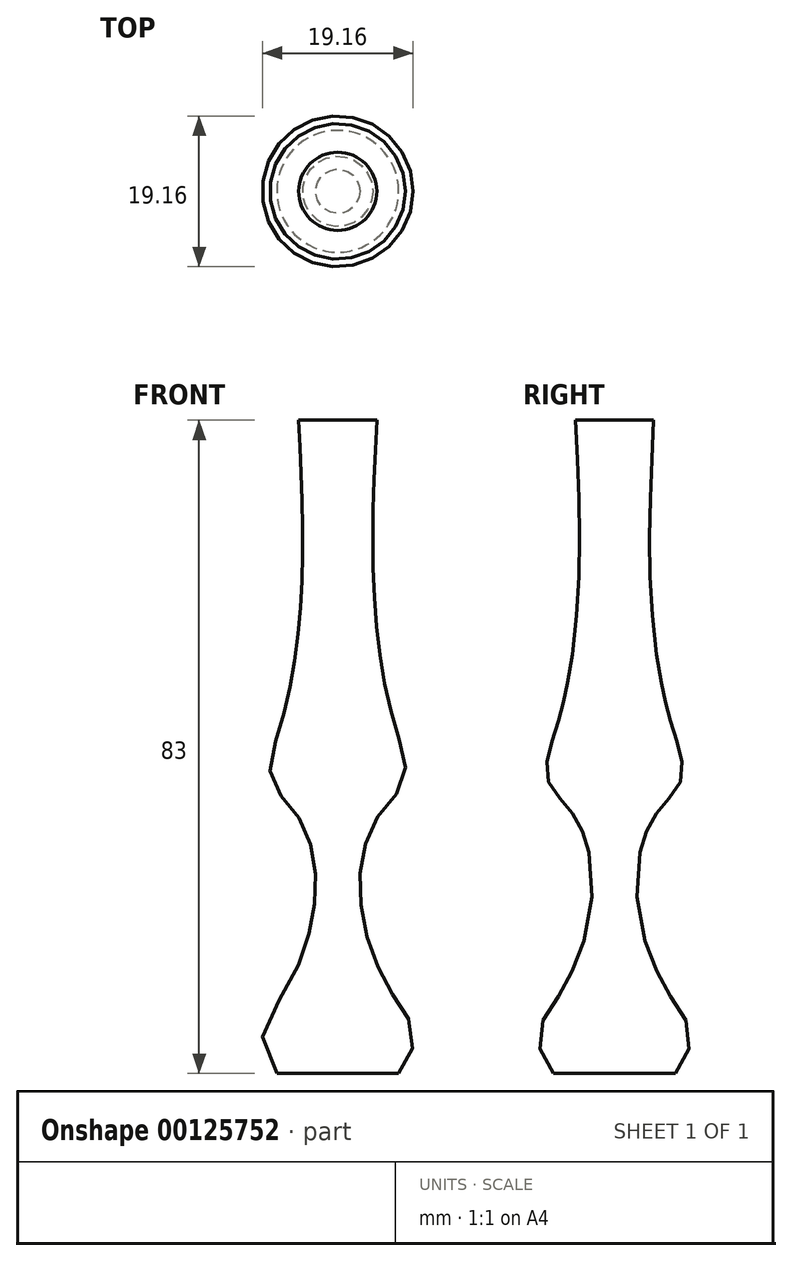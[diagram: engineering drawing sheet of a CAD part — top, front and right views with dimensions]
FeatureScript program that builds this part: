
annotation { "Feature Type Name" : "Feature", "Feature Type Description" : "" }
export const myFeature = defineFeature(function(context is Context, id is Id, definition is map)
    precondition{}
    {
        {
            var Q0;
            Q0=qCreatedBy(makeId("Top.planeOp"),FACE);
            cPlane(context, id + "F0", {"entities" : qUnion([Q0]), "cplaneType" : CPlaneType.OFFSET, "offset" : 50 * mm, "oppositeDirection" : true, "width" : 152.4 * mm, "height" : 152.4 * mm});
        }
        {
            var Q0;
            Q0=qCreatedBy(id+"F0.planeOp",FACE);
            cPlane(context, id + "F1", {"entities" : qUnion([Q0]), "cplaneType" : CPlaneType.OFFSET, "offset" : 2 * mm, "width" : 150 * mm, "height" : 150 * mm});
        }
        {
            var Q0;
            Q0=qCreatedBy(id+"F1.planeOp",FACE);
            cPlane(context, id + "F2", {"entities" : qUnion([Q0]), "cplaneType" : CPlaneType.OFFSET, "offset" : 5 * mm, "width" : 150 * mm, "height" : 150 * mm});
        }
        {
            var Q0;
            Q0=qCreatedBy(id+"F2.planeOp",FACE);
            cPlane(context, id + "F3", {"entities" : qUnion([Q0]), "cplaneType" : CPlaneType.OFFSET, "offset" : 2 * mm, "width" : 150 * mm, "height" : 150 * mm});
        }
        {
            var Q0;
            Q0=qCreatedBy(id+"F3.planeOp",FACE);
            cPlane(context, id + "F4", {"entities" : qUnion([Q0]), "cplaneType" : CPlaneType.OFFSET, "offset" : 25 * mm, "width" : 150 * mm, "height" : 150 * mm});
        }
        {
            var Q0;
            Q0=qCreatedBy(id+"F4.planeOp",FACE);
            cPlane(context, id + "F5", {"entities" : qUnion([Q0]), "cplaneType" : CPlaneType.OFFSET, "offset" : 3 * mm, "width" : 150 * mm, "height" : 150 * mm});
        }
        {
            var Q0;
            Q0=qCreatedBy(id+"F5.planeOp",FACE);
            cPlane(context, id + "F6", {"entities" : qUnion([Q0]), "cplaneType" : CPlaneType.OFFSET, "offset" : 3 * mm, "width" : 150 * mm, "height" : 150 * mm});
        }
        {
            var Q0;
            Q0=qCreatedBy(id+"F6.planeOp",FACE);
            cPlane(context, id + "F7", {"entities" : qUnion([Q0]), "cplaneType" : CPlaneType.OFFSET, "offset" : 3 * mm, "width" : 150 * mm, "height" : 150 * mm});
        }
        {
            var Q0;
            Q0=qCreatedBy(id+"F7.planeOp",FACE);
            cPlane(context, id + "F8", {"entities" : qUnion([Q0]), "cplaneType" : CPlaneType.OFFSET, "offset" : 40 * mm, "width" : 150 * mm, "height" : 150 * mm});
        }
        {
            var Q0;
            Q0=qCreatedBy(id+"F0.planeOp",FACE);
            var sketch = newSketch(context, id + "F9", { "sketchPlane" : qUnion([Q0])});
            skCircle(sketch, "E0", {"center": v(0, 0) * mm, "radius": 7.73 * mm});
            skSolve(sketch);
        }
        {
            var Q0;
            Q0=qCreatedBy(id+"F1.planeOp",FACE);
            var sketch = newSketch(context, id + "F10", { "sketchPlane" : qUnion([Q0])});
            skCircle(sketch, "E1", {"center": v(0, 0) * mm, "radius": 9.1 * mm});
            skSolve(sketch);
        }
        {
            var Q0;
            Q0=qCreatedBy(id+"F2.planeOp",FACE);
            var sketch = newSketch(context, id + "F11", { "sketchPlane" : qUnion([Q0])});
            skCircle(sketch, "E2", {"center": v(0, 0) * mm, "radius": 9 * mm});
            skSolve(sketch);
        }
        {
            var Q0;
            Q0=qCreatedBy(id+"F3.planeOp",FACE);
            var sketch = newSketch(context, id + "F12", { "sketchPlane" : qUnion([Q0])});
            skCircle(sketch, "E3", {"center": v(0, 0) * mm, "radius": 7.68 * mm});
            skSolve(sketch);
        }
        {
            var Q0;
            Q0=qCreatedBy(id+"F4.planeOp",FACE);
            var sketch = newSketch(context, id + "F13", { "sketchPlane" : qUnion([Q0])});
            skCircle(sketch, "E4", {"center": v(0, 0) * mm, "radius": 6.06 * mm});
            skSolve(sketch);
        }
        {
            var Q0;
            Q0=qCreatedBy(id+"F5.planeOp",FACE);
            var sketch = newSketch(context, id + "F14", { "sketchPlane" : qUnion([Q0])});
            skCircle(sketch, "E5", {"center": v(0, 0) * mm, "radius": 8.34 * mm});
            skSolve(sketch);
        }
        {
            var Q0;
            Q0=qCreatedBy(id+"F6.planeOp",FACE);
            var sketch = newSketch(context, id + "F15", { "sketchPlane" : qUnion([Q0])});
            skCircle(sketch, "E6", {"center": v(0, 0) * mm, "radius": 8.5 * mm});
            skSolve(sketch);
        }
        {
            var Q0;
            Q0=qCreatedBy(id+"F7.planeOp",FACE);
            var sketch = newSketch(context, id + "F16", { "sketchPlane" : qUnion([Q0])});
            skCircle(sketch, "E7", {"center": v(0, 0) * mm, "radius": 7.66 * mm});
            skSolve(sketch);
        }
        {
            var Q0;
            Q0=qCreatedBy(id+"F8.planeOp",FACE);
            var sketch = newSketch(context, id + "F17", { "sketchPlane" : qUnion([Q0])});
            skCircle(sketch, "E8", {"center": v(0, 0) * mm, "radius": 4.96 * mm});
            skSolve(sketch);
        }
        {
            var Q0;
            Q0 = qSketchRegion(id + "F9", true);
            var Q1;
            Q1 = qSketchRegion(id + "F10", true);
            var Q2;
            Q2 = qSketchRegion(id + "F11", true);
            var Q3;
            Q3 = qSketchRegion(id + "F12", true);
            var Q4;
            Q4 = qSketchRegion(id + "F13", true);
            var Q5;
            Q5 = qSketchRegion(id + "F14", true);
            var Q6;
            Q6 = qSketchRegion(id + "F15", true);
            var Q7;
            Q7 = qSketchRegion(id + "F16", true);
            var Q8;
            Q8 = qSketchRegion(id + "F17", true);
            loft(context, id + "F18", {"sheetProfilesArray" : [{ "sheetProfileEntities" : qUnion([Q0]) }, { "sheetProfileEntities" : qUnion([Q1]) }, { "sheetProfileEntities" : qUnion([Q2]) }, { "sheetProfileEntities" : qUnion([Q3]) }, { "sheetProfileEntities" : qUnion([Q4]) }, { "sheetProfileEntities" : qUnion([Q5]) }, { "sheetProfileEntities" : qUnion([Q6]) }, { "sheetProfileEntities" : qUnion([Q7]) }, { "sheetProfileEntities" : qUnion([Q8]) }]});
        }
    });
